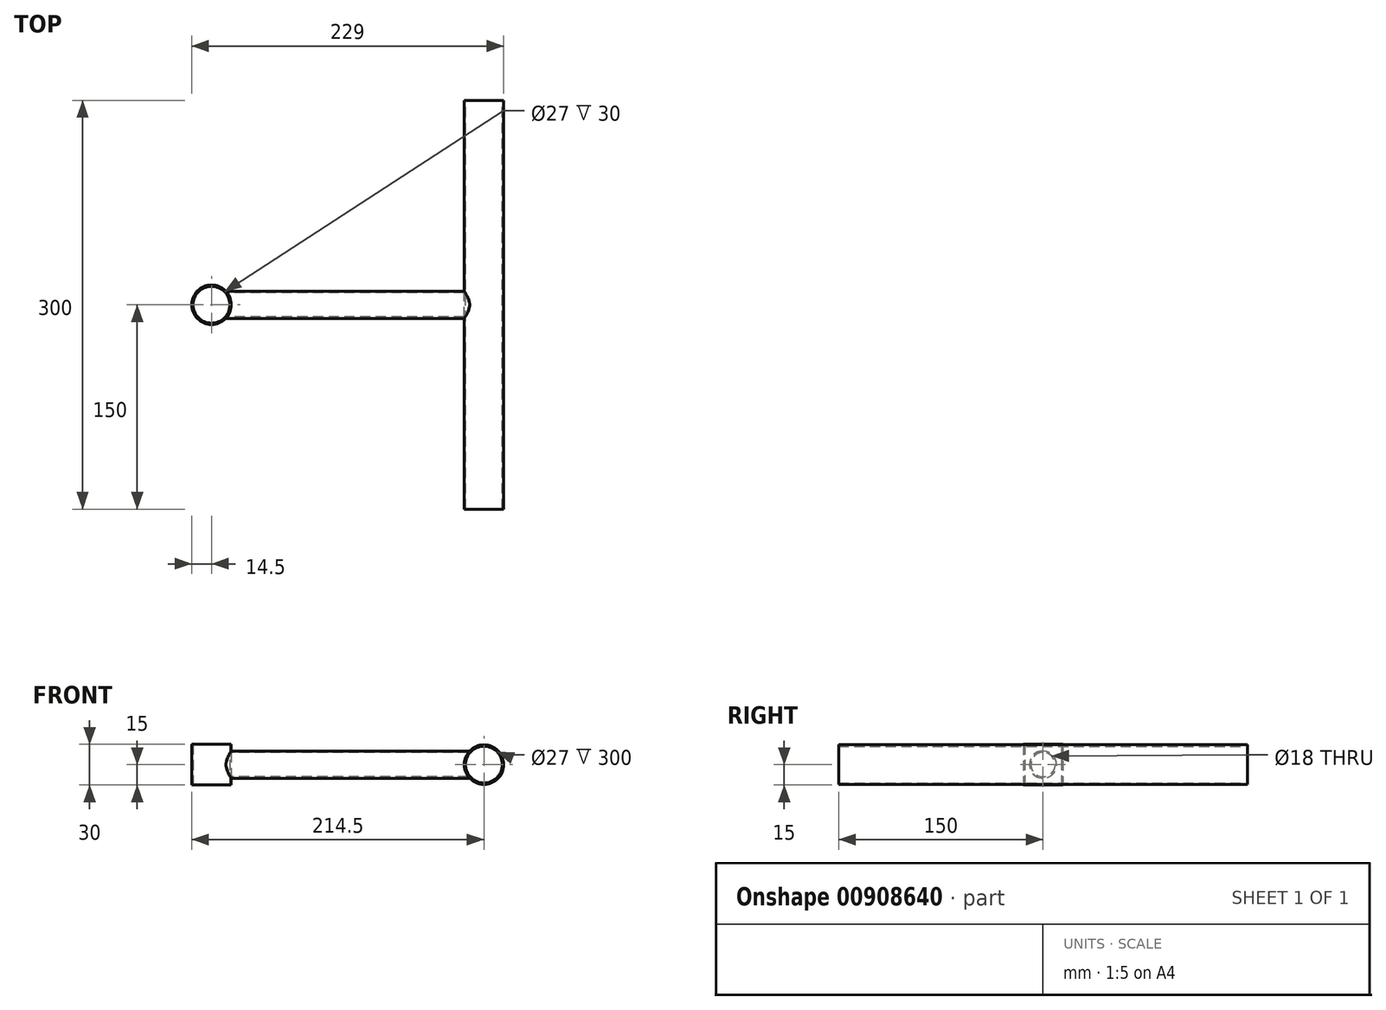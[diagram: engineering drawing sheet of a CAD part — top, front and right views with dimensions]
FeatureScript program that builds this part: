
annotation { "Feature Type Name" : "Feature", "Feature Type Description" : "" }
export const myFeature = defineFeature(function(context is Context, id is Id, definition is map)
    precondition{}
    {
        {
            var Q0;
            Q0=qCreatedBy(makeId("Top.planeOp"),FACE);
            var sketch = newSketch(context, id + "F0", { "sketchPlane" : qUnion([Q0])});
            skCircle(sketch, "E0", {"center": v(0, 0) * mm, "radius": 13.5 * mm});
            skCircle(sketch, "E1", {"center": v(0, 0) * mm, "radius": 14.5 * mm});
            skSolve(sketch);
        }
        {
            var Q0;
            Q0 = qSketchRegion(id + "F0", true);
            extrude(context, id + "F1", {"entities" : qUnion([Q0]), "depth" : 30 * mm, "offsetDistance" : 25 * mm});
        }
        {
            var Q0;
            Q0=qCreatedBy(makeId("Right.planeOp"),FACE);
            var sketch = newSketch(context, id + "F2", { "sketchPlane" : qUnion([Q0])});
            skLineSegment(sketch, "E2", {"start": v(0, 0) * mm, "end": v(0, 15) * mm});
            skCircle(sketch, "E3", {"center": v(0, 15) * mm, "radius": 9 * mm});
            skCircle(sketch, "E4", {"center": v(0, 15) * mm, "radius": 10 * mm});
            skSolve(sketch);
        }
        {
            var Q0;
            Q0 = qSketchRegion(id + "F2", true);
            extrude(context, id + "F3", {"entities" : qUnion([Q0]), "operationType" : NewBodyOperationType.ADD, "depth" : 200 * mm, "offsetDistance" : 25 * mm});
        }
        {
            var Q0;
            Q0=makeQuery(id+"F3.opExtrude","CAP_FACE",FACE,{"disambiguationData":[OSD([sQuery(id+"F2.wireOp",EDGE,"E3"),sQuery(id+"F2.wireOp",EDGE,"E4")])],"isStart":true});
            var Q1;
            {var subQ1=sQuery(id+"F0.wireOp",EDGE,"E0");Q1=makeQuery(id+"F3.boolean.opBoolean","SPLIT",FACE,{"disambiguationData":[TD([makeQuery(id+"F3.opExtrude","SWEPT_FACE",FACE,{"disambiguationData":[OSD([sQuery(id+"F2.wireOp",EDGE,"E4")])]})])],"derivedFrom":makeQuery(id+"F1.opExtrude","SWEPT_FACE",FACE,{"disambiguationData":[OSD([subQ1])]})});}
            extrude(context, id + "F4", {"entities" : qUnion([Q0]), "operationType" : NewBodyOperationType.REMOVE, "endBound" : BoundingType.UP_TO_SURFACE, "oppositeDirection" : true, "depth" : 25 * mm, "endBoundEntityFace" : qUnion([Q1]), "offsetDistance" : 25 * mm});
        }
        {
            var Q0;
            Q0=qCreatedBy(makeId("Front.planeOp"),FACE);
            var sketch = newSketch(context, id + "F5", { "sketchPlane" : qUnion([Q0])});
            skLineSegment(sketch, "E5", {"start": v(0, 0) * mm, "end": v(0, 15) * mm});
            skLineSegment(sketch, "E6", {"start": v(0, 15) * mm, "end": v(200, 15) * mm});
            skCircle(sketch, "E7", {"center": v(200, 15) * mm, "radius": 13.5 * mm});
            skCircle(sketch, "E8", {"center": v(200, 15) * mm, "radius": 14.5 * mm});
            skSolve(sketch);
        }
        {
            var Q0;
            Q0 = qSketchRegion(id + "F5", true);
            extrude(context, id + "F6", {"entities" : qUnion([Q0]), "operationType" : NewBodyOperationType.ADD, "depth" : 150 * mm, "offsetDistance" : 25 * mm});
        }
        {
            var Q0;
            Q0=makeQuery(id+"F1.opExtrude","SWEPT_BODY",BODY,{"disambiguationData":[OSD([sQuery(id+"F0.wireOp",EDGE,"E0"),sQuery(id+"F0.wireOp",EDGE,"E1")])]});
            var Q1;
            Q1=qCreatedBy(makeId("Front.planeOp"),FACE);
            mirror(context, id + "F7", {"operationType" : NewBodyOperationType.ADD, "entities" : qUnion([Q0]), "mirrorPlane" : qUnion([Q1])});
        }
        {
            var Q0;
            Q0=makeQuery(id+"F3.opExtrude","CAP_FACE",FACE,{"disambiguationData":[OSD([sQuery(id+"F2.wireOp",EDGE,"E3"),sQuery(id+"F2.wireOp",EDGE,"E4")])],"isStart":false});
            var Q1;
            {var subQ1=sQuery(id+"F5.wireOp",EDGE,"E7");var subQ2=makeQuery(id+"F6.boolean.opBoolean","SPLIT",FACE,{"disambiguationData":[TD([makeQuery(id+"F3.opExtrude","SWEPT_FACE",FACE,{"disambiguationData":[OSD([sQuery(id+"F2.wireOp",EDGE,"E4")])]})])],"derivedFrom":makeQuery(id+"F6.opExtrude","SWEPT_FACE",FACE,{"disambiguationData":[OSD([subQ1])]})});Q1=makeQuery(id+"F7.boolean.opBoolean","MERGE",FACE,{"derivedFrom":[subQ2,makeQuery(id+"F7.opPattern","COPY",FACE,{"derivedFrom":subQ2,"instanceName":"1"})]});}
            extrude(context, id + "F8", {"entities" : qUnion([Q0]), "operationType" : NewBodyOperationType.REMOVE, "endBound" : BoundingType.UP_TO_SURFACE, "oppositeDirection" : true, "depth" : 25 * mm, "endBoundEntityFace" : qUnion([Q1]), "offsetDistance" : 25 * mm});
        }
    });
